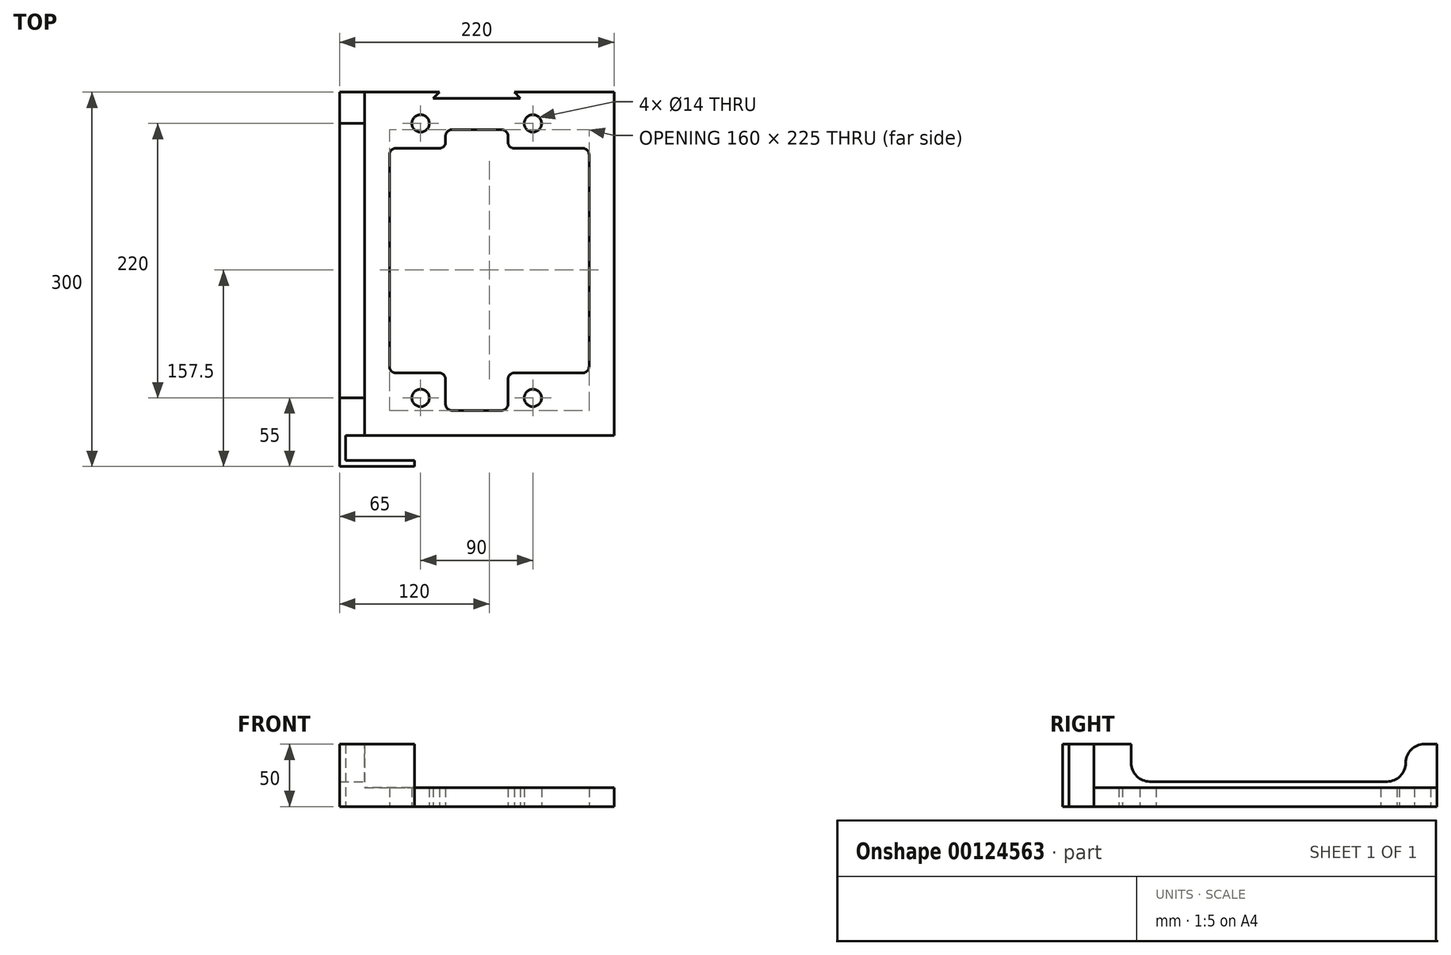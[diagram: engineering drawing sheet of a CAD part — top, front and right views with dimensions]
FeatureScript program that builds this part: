
annotation { "Feature Type Name" : "Feature", "Feature Type Description" : "" }
export const myFeature = defineFeature(function(context is Context, id is Id, definition is map)
    precondition{}
    {
        {
            var Q0;
            Q0=qCreatedBy(makeId("Top.planeOp"),FACE);
            var sketch = newSketch(context, id + "F0", { "sketchPlane" : qUnion([Q0])});
            skLineSegment(sketch, "E0", {"start": v(0, 0) * mm, "end": v(60, 0) * mm});
            skLineSegment(sketch, "E1", {"start": v(60, 0) * mm, "end": v(60, 5) * mm});
            skLineSegment(sketch, "E2", {"start": v(60, 5) * mm, "end": v(5, 5) * mm});
            skLineSegment(sketch, "E3", {"start": v(5, 5) * mm, "end": v(5, 25) * mm});
            skLineSegment(sketch, "E4", {"start": v(5, 25) * mm, "end": v(220, 25) * mm});
            skLineSegment(sketch, "E5", {"start": v(220, 25) * mm, "end": v(220, 300) * mm});
            skLineSegment(sketch, "E6", {"start": v(140, 300) * mm, "end": v(145, 295) * mm});
            skLineSegment(sketch, "E7", {"start": v(145, 295) * mm, "end": v(75, 295) * mm});
            skLineSegment(sketch, "E8", {"start": v(75, 295) * mm, "end": v(80, 300) * mm});
            skLineSegment(sketch, "E9", {"start": v(0, 300) * mm, "end": v(0, 0) * mm});
            skLineSegment(sketch, "E10", {"start": v(140, 300) * mm, "end": v(220, 300) * mm});
            skLineSegment(sketch, "E11", {"start": v(80, 300) * mm, "end": v(0, 300) * mm});
            skLineSegment(sketch, "E12", {"start": v(110, 295) * mm, "end": v(110, 25) * mm, "construction": true});
            skLineSegment(sketch, "E13", {"start": v(65, 55) * mm, "end": v(155, 55) * mm, "construction": true});
            skPoint(sketch, "E14", {"position": v(110, 55) * mm});
            skCircle(sketch, "E15", {"center": v(65, 55) * mm, "radius": 7 * mm});
            skCircle(sketch, "E16", {"center": v(155, 55) * mm, "radius": 7 * mm});
            skPoint(sketch, "E17", {"position": v(110, 275) * mm});
            skCircle(sketch, "E18", {"center": v(65, 275) * mm, "radius": 7 * mm});
            skCircle(sketch, "E19", {"center": v(155, 275) * mm, "radius": 7 * mm});
            skLineSegment(sketch, "E20", {"start": v(20, 300) * mm, "end": v(20, 25) * mm});
            skLineSegment(sketch, "E21.left", {"start": v(40, 255) * mm, "end": v(40, 75) * mm});
            skLineSegment(sketch, "E21.right", {"start": v(200, 255) * mm, "end": v(200, 75) * mm});
            skLineSegment(sketch, "E22", {"start": v(40, 255) * mm, "end": v(85, 255) * mm});
            skLineSegment(sketch, "E23", {"start": v(85, 255) * mm, "end": v(85, 270) * mm});
            skLineSegment(sketch, "E24", {"start": v(85, 270) * mm, "end": v(135, 270) * mm});
            skLineSegment(sketch, "E25", {"start": v(135, 270) * mm, "end": v(135, 255) * mm});
            skLineSegment(sketch, "E26", {"start": v(135, 255) * mm, "end": v(200, 255) * mm});
            skLineSegment(sketch, "E27", {"start": v(40, 75) * mm, "end": v(85, 75) * mm});
            skLineSegment(sketch, "E28", {"start": v(85, 75) * mm, "end": v(85, 45) * mm});
            skLineSegment(sketch, "E29", {"start": v(135, 45) * mm, "end": v(135, 75) * mm});
            skLineSegment(sketch, "E30", {"start": v(135, 75) * mm, "end": v(200, 75) * mm});
            skLineSegment(sketch, "E31", {"start": v(65, 275) * mm, "end": v(155, 275) * mm, "construction": true});
            skLineSegment(sketch, "E32", {"start": v(85, 45) * mm, "end": v(135, 45) * mm});
            skLineSegment(sketch, "E33", {"start": v(20, 304.73) * mm, "end": v(90.17, 304.73) * mm});
            skLineSegment(sketch, "E34", {"start": v(90.17, 304.73) * mm, "end": v(83.39, 297.95) * mm});
            skLineSegment(sketch, "E35", {"start": v(83.39, 297.95) * mm, "end": v(135.3, 297.95) * mm});
            skLineSegment(sketch, "E36", {"start": v(135.3, 297.95) * mm, "end": v(128.51, 304.73) * mm});
            skLineSegment(sketch, "E37", {"start": v(128.51, 304.73) * mm, "end": v(220, 304.73) * mm});
            skLineSegment(sketch, "E38", {"start": v(220, 304.73) * mm, "end": v(220, 497.7) * mm});
            skLineSegment(sketch, "E39", {"start": v(220, 497.7) * mm, "end": v(0, 497.7) * mm});
            skLineSegment(sketch, "E40", {"start": v(0, 497.7) * mm, "end": v(0, 304.73) * mm});
            skLineSegment(sketch, "E41", {"start": v(0, 304.73) * mm, "end": v(20, 304.73) * mm});
            skLineSegment(sketch, "E42", {"start": v(20, 304.73) * mm, "end": v(20, 497.7) * mm});
            skSolve(sketch);
        }
        {
            var Q0;
            Q0=makeQuery(id+"F0.imprint","IMPRINT",FACE,{"disambiguationData":[TD([[makeQuery(id+"F0.imprint","IMPRINT",EDGE,{"derivedFrom":sQuery(id+"F0.wireOp",EDGE,"E0")}),1.0]])]});
            var Q1;
            {var subQ3=sQuery(id+"F0.wireOp",EDGE,"E5");Q1=makeQuery(id+"F0.imprint","IMPRINT",FACE,{"disambiguationData":[TD([[makeQuery(id+"F0.imprint","IMPRINT",EDGE,{"derivedFrom":subQ3}),1.0]])]});}
            extrude(context, id + "F1", {"entities" : qUnion([Q0, Q1]), "depth" : 15 * mm});
        }
        {
            var Q0;
            Q0=makeQuery(id+"F0.imprint","IMPRINT",FACE,{"disambiguationData":[TD([[makeQuery(id+"F0.imprint","IMPRINT",EDGE,{"derivedFrom":sQuery(id+"F0.wireOp",EDGE,"E0")}),1.0]])]});
            extrude(context, id + "F2", {"entities" : qUnion([Q0]), "operationType" : NewBodyOperationType.ADD, "depth" : 50 * mm});
        }
        {
            var Q0;
            Q0=makeQuery(id+"F2.opExtrude","SWEPT_FACE",FACE,{"disambiguationData":[OSD([sQuery(id+"F0.wireOp",EDGE,"E20")])]});
            var sketch = newSketch(context, id + "F3", { "sketchPlane" : qUnion([Q0])});
            skLineSegment(sketch, "E43", {"start": v(275, 50) * mm, "end": v(275, 20) * mm});
            skLineSegment(sketch, "E44", {"start": v(275, 20) * mm, "end": v(55, 20) * mm});
            skLineSegment(sketch, "E45", {"start": v(55, 20) * mm, "end": v(55, 50) * mm});
            skSolve(sketch);
        }
        {
            var Q0;
            {var subQ0=sQuery(id+"F3.wireOp",EDGE,"E43");Q0=makeQuery(id+"F3.imprint","IMPRINT",FACE,{"disambiguationData":[TD([[makeQuery(id+"F3.imprint","IMPRINT",EDGE,{"derivedFrom":subQ0}),-1.0]])]});}
            extrude(context, id + "F4", {"entities" : qUnion([Q0]), "operationType" : NewBodyOperationType.REMOVE, "oppositeDirection" : true, "depth" : 25 * mm});
        }
        {
            var Q0;
            Q0=makeQuery(id+"F4.boolean.opBoolean","COPY",EDGE,{"derivedFrom":makeQuery(id+"F4.opExtrude","SWEPT_EDGE",EDGE,{"disambiguationData":[OSD([sQuery(id+"F3.wireOp",EDGE,"E43"),sQuery(id+"F3.wireOp",EDGE,"E44")])]})});
            var Q1;
            Q1=makeQuery(id+"F4.boolean.opBoolean","COPY",EDGE,{"derivedFrom":makeQuery(id+"F4.opExtrude","SWEPT_EDGE",EDGE,{"disambiguationData":[OSD([sQuery(id+"F3.wireOp",EDGE,"E44"),sQuery(id+"F3.wireOp",EDGE,"E45")])]})});
            var Q2;
            Q2=makeQuery(id+"F4.boolean.opBoolean","COPY",EDGE,{"derivedFrom":makeQuery(id+"F4.opExtrude","SWEPT_EDGE",EDGE,{"disambiguationData":[OSD([sQuery(id+"F0.wireOp",EDGE,"E20"),sQuery(id+"F3.wireOp",EDGE,"E43")])]})});
            var Q3;
            Q3=makeQuery(id+"F4.boolean.opBoolean","COPY",EDGE,{"derivedFrom":makeQuery(id+"F4.opExtrude","SWEPT_EDGE",EDGE,{"disambiguationData":[OSD([sQuery(id+"F0.wireOp",EDGE,"E20"),sQuery(id+"F3.wireOp",EDGE,"E45")])]})});
            fillet(context, id + "F5", {"entities" : qUnion([Q0, Q1, Q2, Q3]), "radius" : 15 * mm, "tangentPropagation" : true, "allowEdgeOverflow" : false});
        }
        {
            var Q0;
            Q0=makeQuery(id+"F1.opExtrude","SWEPT_EDGE",EDGE,{"disambiguationData":[OSD([sQuery(id+"F0.wireOp",EDGE,"E21.bottom"),sQuery(id+"F0.wireOp",EDGE,"E21.left")])]});
            var Q1;
            Q1=makeQuery(id+"F1.opExtrude","SWEPT_EDGE",EDGE,{"disambiguationData":[OSD([sQuery(id+"F0.wireOp",EDGE,"E21.bottom"),sQuery(id+"F0.wireOp",EDGE,"E21.right")])]});
            var Q2;
            Q2=makeQuery(id+"F1.opExtrude","SWEPT_EDGE",EDGE,{"disambiguationData":[OSD([sQuery(id+"F0.wireOp",EDGE,"E21.top"),sQuery(id+"F0.wireOp",EDGE,"E21.right")])]});
            var Q3;
            Q3=makeQuery(id+"F1.opExtrude","SWEPT_EDGE",EDGE,{"disambiguationData":[OSD([sQuery(id+"F0.wireOp",EDGE,"E21.top"),sQuery(id+"F0.wireOp",EDGE,"E21.left")])]});
            var Q4;
            Q4=makeQuery(id+"F1.opExtrude","SWEPT_EDGE",EDGE,{"disambiguationData":[OSD([sQuery(id+"F0.wireOp",EDGE,"E27"),sQuery(id+"F0.wireOp",EDGE,"E28")])]});
            var Q5;
            Q5=makeQuery(id+"F1.opExtrude","SWEPT_EDGE",EDGE,{"disambiguationData":[OSD([sQuery(id+"F0.wireOp",EDGE,"E29"),sQuery(id+"F0.wireOp",EDGE,"E30")])]});
            var Q6;
            Q6=makeQuery(id+"F1.opExtrude","SWEPT_EDGE",EDGE,{"disambiguationData":[OSD([sQuery(id+"F0.wireOp",EDGE,"E28"),sQuery(id+"F0.wireOp",EDGE,"E32")])]});
            var Q7;
            Q7=makeQuery(id+"F1.opExtrude","SWEPT_EDGE",EDGE,{"disambiguationData":[OSD([sQuery(id+"F0.wireOp",EDGE,"E29"),sQuery(id+"F0.wireOp",EDGE,"E32")])]});
            var Q8;
            Q8=makeQuery(id+"F1.opExtrude","SWEPT_EDGE",EDGE,{"disambiguationData":[OSD([sQuery(id+"F0.wireOp",EDGE,"E22"),sQuery(id+"F0.wireOp",EDGE,"E23")])]});
            var Q9;
            Q9=makeQuery(id+"F1.opExtrude","SWEPT_EDGE",EDGE,{"disambiguationData":[OSD([sQuery(id+"F0.wireOp",EDGE,"E23"),sQuery(id+"F0.wireOp",EDGE,"E24")])]});
            var Q10;
            Q10=makeQuery(id+"F1.opExtrude","SWEPT_EDGE",EDGE,{"disambiguationData":[OSD([sQuery(id+"F0.wireOp",EDGE,"E25"),sQuery(id+"F0.wireOp",EDGE,"E26")])]});
            var Q11;
            Q11=makeQuery(id+"F1.opExtrude","SWEPT_EDGE",EDGE,{"disambiguationData":[OSD([sQuery(id+"F0.wireOp",EDGE,"E24"),sQuery(id+"F0.wireOp",EDGE,"E25")])]});
            fillet(context, id + "F6", {"entities" : qUnion([Q0, Q1, Q2, Q3, Q4, Q5, Q6, Q7, Q8, Q9, Q10, Q11]), "radius" : 5 * mm, "tangentPropagation" : true, "allowEdgeOverflow" : false});
        }
    });
